# Revit family: 28L 4 to 12 units back to back indoor manifold system ff
name_source: partatom
category: Plumbing Fixtures
revit_build: Autodesk Revit 2017 (Build: 20160225_1515(x64)
units: mm (PartAtom-declared; Revit-internal decimal feet)

## family parameters
Always vertical = Yes
Cut with Voids When Loaded = No
Part Type = Normal
Room Calculation Point = No
Round Connector Dimension = Use Diameter
Shared = No
Work Plane-Based = No

## types (5) — shared parameters
Base Support L = Yes
Cold Water Inlet Pipe connector description = Male threaded connector R1-1/2"
Cold Water Inlet Pipe diameter = 38.1mm(DN 40)
Exhaust Air pipe connector description = 80-125mm coaxial air connector
Exhaust Air pipe connector system classification = Exhaust Air
Exhaust Air pipe diameter = 125.000 mm
Gas Inlet Pipe connector description = Male threaded connector R1-1/2"
Gas Inlet Pipe diameter = 38.1mm(DN 40)
Hot Water Outlet Pipe connector description = Male threaded connector R1-1/2"
Hot Water Outlet Pipe diameter = 38.1mm(DN 40)
Nominal depth = 900mm
Nominal height = 1540mm
Supply Air/Air Inlet connector classification = Supply Air
Supply Air/Air Inlet pipe connector description = 80-125mm coaxial air connector
Supply Air/Air Inlet pipe diameter = 80.000 mm
Unit Offset = 41.300 mm

## per-type parameters (varying)
- 28L 4 units Back to back indoor: 2 Unit L=Yes; 2 Unit R=No; 3 Unit L=No; 3 Unit R=No; Array Offset=360.000 mm; Base Offset L=794.000 mm; Base Offset R=1040.000 mm; Base Support R=No; Connector Left=784.000 mm; Connector Right=1550.000 mm; D1=1757.000 mm; D2=1757.000 mm; D3=1757.000 mm; No of Connectors 1=2; No of Connectors 2=2; No. of power supply point required=4; Nominal width=794mm; Number of Gas Water Heaters=4; Product SKU Dux brand=D42800FN/LBx; Product SKU Thermann brand=T42800FN/LBx; Product description=Gas Water heater Manifold 4 units indoor back to back; Total Max. power requirement=772W; Total nominal gas consumption (MJ/h)=820; Total number of exhaust air connections=4; Total number of supply air connections=4; Weight (Kg)=180
- 28L 6 units Back to back indoor: 2 Unit L=No; 2 Unit R=No; 3 Unit L=Yes; 3 Unit R=No; Array Offset=720.000 mm; Base Offset L=1170.000 mm; Base Offset R=1040.000 mm; Base Support R=No; Connector Left=1160.000 mm; Connector Right=1550.000 mm; D1=1765.000 mm; D2=1765.000 mm; D3=1765.000 mm; No of Connectors 1=3; No of Connectors 2=3; No. of power supply point required=6; Nominal width=1170mm; Number of Gas Water Heaters=6; Product SKU Dux brand=D62800FN/LBx; Product SKU Thermann brand=T62800FN/LBx; Product description=Gas Water heater Manifold 6 units indoor back to back; Total Max. power requirement=1158W; Total nominal gas consumption (MJ/h)=1230; Total number of exhaust air connections=6; Total number of supply air connections=6; Weight (Kg)=240
- 28L 8 units Back to back indoor: 2 Unit L=Yes; 2 Unit R=Yes; 3 Unit L=No; 3 Unit R=No; Array Offset=360.000 mm; Base Offset L=794.000 mm; Base Offset R=794.000 mm; Base Support R=Yes; Connector Left=784.000 mm; Connector Right=756.000 mm; D1=963.000 mm; D2=963.000 mm; D3=1757.000 mm; No of Connectors 1=2; No of Connectors 2=2; No. of power supply point required=8; Nominal width=1588mm; Number of Gas Water Heaters=8; Product SKU Dux brand=D82800FN/LBx; Product SKU Thermann brand=T82800FN/LBx; Product description=Gas Water heater Manifold 8 units indoor back to back; Total Max. power requirement=1556W; Total nominal gas consumption (MJ/h)=1640; Total number of exhaust air connections=8; Total number of supply air connections=8; Weight (Kg)=360
- 28L 10 units Back to back indoor: 2 Unit L=No; 2 Unit R=Yes; 3 Unit L=Yes; 3 Unit R=No; Array Offset=1522.000 mm; Base Offset L=1170.000 mm; Base Offset R=794.000 mm; Base Support R=Yes; Connector Left=1160.000 mm; Connector Right=756.000 mm; D1=963.000 mm; D2=963.000 mm; D3=1765.000 mm; No of Connectors 1=2; No of Connectors 2=3; No. of power supply point required=10; Nominal width=1964mm; Number of Gas Water Heaters=10; Product SKU Dux brand=D102800FN/LBx; Product SKU Thermann brand=T102800FN/LBx; Product description=Gas Water heater Manifold 10 units indoor back to back; Total Max. power requirement=1942W; Total nominal gas consumption (MJ/h)=2050; Total number of exhaust air connections=10; Total number of supply air connections=10; Weight (Kg)=420
- 28L 12 units Back to back indoor: 2 Unit L=No; 2 Unit R=No; 3 Unit L=Yes; 3 Unit R=Yes; Array Offset=1170.000 mm; Base Offset L=1170.000 mm; Base Offset R=1170.000 mm; Base Support R=Yes; Connector Left=1160.000 mm; Connector Right=380.000 mm; D1=1315.000 mm; D2=595.000 mm; D3=1765.000 mm; No of Connectors 1=3; No of Connectors 2=3; No. of power supply point required=12; Nominal width=2340mm; Number of Gas Water Heaters=12; Product SKU Dux brand=D122800FN/LBx; Product SKU Thermann brand=T122800FN/LBx; Product description=Gas Water heater Manifold 12 units indoor back to back; Total Max. power requirement=2328W; Total nominal gas consumption (MJ/h)=2460; Total number of exhaust air connections=12; Total number of supply air connections=12; Weight (Kg)=480

## geometry (parser evidence)
native form markers: Sweep x17
no freeform markers — native parametric forms only
